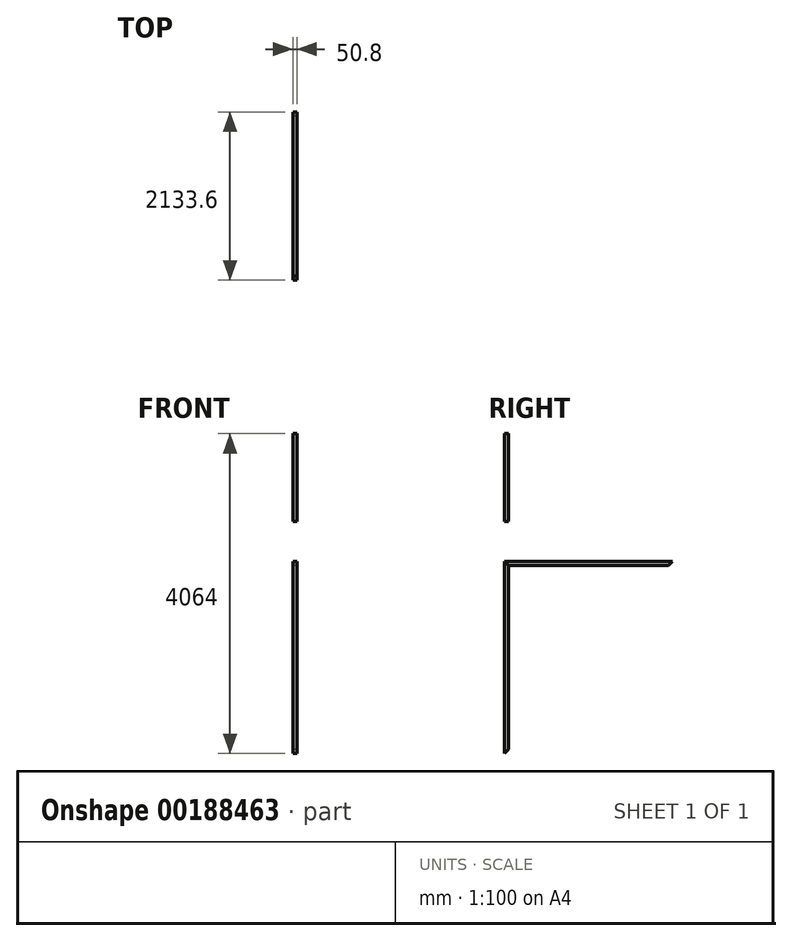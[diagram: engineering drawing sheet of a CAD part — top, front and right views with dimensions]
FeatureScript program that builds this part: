
annotation { "Feature Type Name" : "Feature", "Feature Type Description" : "" }
export const myFeature = defineFeature(function(context is Context, id is Id, definition is map)
    precondition{}
    {
        {
            var Q0;
            Q0=qCreatedBy(makeId("Right.planeOp"),FACE);
            var sketch = newSketch(context, id + "F0", { "sketchPlane" : qUnion([Q0])});
            skLineSegment(sketch, "E0.bottom", {"start": v(0, 0) * mm, "end": v(2133.6, 0) * mm});
            skLineSegment(sketch, "E0.top", {"start": v(50.8, 50.8) * mm, "end": v(2082.8, 50.8) * mm});
            skLineSegment(sketch, "E1", {"start": v(2133.6, 0) * mm, "end": v(2133.6, 2438.4) * mm});
            skLineSegment(sketch, "E2", {"start": v(2082.8, 2387.6) * mm, "end": v(2082.8, 50.8) * mm});
            skLineSegment(sketch, "E3", {"start": v(2082.8, 50.8) * mm, "end": v(2133.6, 0) * mm});
            skLineSegment(sketch, "E4", {"start": v(50.8, 50.8) * mm, "end": v(50.8, 2387.6) * mm});
            skLineSegment(sketch, "E5", {"start": v(0, 0) * mm, "end": v(50.8, 50.8) * mm});
            skLineSegment(sketch, "E6", {"start": v(0, 0) * mm, "end": v(0, 2438.4) * mm});
            skLineSegment(sketch, "E7", {"start": v(50.8, 2387.6) * mm, "end": v(2082.8, 2387.6) * mm});
            skLineSegment(sketch, "E8", {"start": v(2082.8, 2387.6) * mm, "end": v(2133.6, 2438.4) * mm});
            skLineSegment(sketch, "E9", {"start": v(50.8, 2387.6) * mm, "end": v(0, 2438.4) * mm});
            skLineSegment(sketch, "E10", {"start": v(0, 2438.4) * mm, "end": v(2133.6, 2438.4) * mm});
            skLineSegment(sketch, "E11", {"start": v(50.8, 1193.8) * mm, "end": v(2082.8, 1193.8) * mm});
            skLineSegment(sketch, "E12", {"start": v(50.8, 1244.6) * mm, "end": v(2082.8, 1244.6) * mm});
            skLineSegment(sketch, "E13", {"start": v(2590.8, 0) * mm, "end": v(2590.8, 2438.4) * mm});
            skLineSegment(sketch, "E14", {"start": v(2590.8, 2438.4) * mm, "end": v(3810, 2438.4) * mm});
            skLineSegment(sketch, "E15", {"start": v(3810, 2438.4) * mm, "end": v(3810, 0) * mm});
            skLineSegment(sketch, "E16", {"start": v(3810, 0) * mm, "end": v(2590.8, 0) * mm});
            skLineSegment(sketch, "E17.bottom", {"start": v(2641.6, 2387.6) * mm, "end": v(3759.2, 2387.6) * mm});
            skLineSegment(sketch, "E17.top", {"start": v(2641.6, 50.8) * mm, "end": v(3759.2, 50.8) * mm});
            skLineSegment(sketch, "E17.left", {"start": v(2641.6, 2438.4) * mm, "end": v(2641.6, 0) * mm});
            skLineSegment(sketch, "E17.right", {"start": v(3759.2, 2438.4) * mm, "end": v(3759.2, 0) * mm});
            skLineSegment(sketch, "E18", {"start": v(0, 2895.6) * mm, "end": v(2133.6, 2895.6) * mm});
            skLineSegment(sketch, "E19", {"start": v(0, 2895.6) * mm, "end": v(0, 4114.8) * mm});
            skLineSegment(sketch, "E20", {"start": v(0, 4114.8) * mm, "end": v(2133.6, 4114.8) * mm});
            skLineSegment(sketch, "E21", {"start": v(2133.6, 4114.8) * mm, "end": v(2133.6, 2895.6) * mm});
            skLineSegment(sketch, "E22.bottom", {"start": v(0, 4064) * mm, "end": v(2133.6, 4064) * mm});
            skLineSegment(sketch, "E22.top", {"start": v(0, 2946.4) * mm, "end": v(2133.6, 2946.4) * mm});
            skLineSegment(sketch, "E22.left", {"start": v(50.8, 4064) * mm, "end": v(50.8, 2946.4) * mm});
            skLineSegment(sketch, "E22.right", {"start": v(2082.8, 4064) * mm, "end": v(2082.8, 2946.4) * mm});
            skText(sketch, "E23", { "text": "Top", "fontName": "OpenSans-Regular.ttf"});
            skText(sketch, "E24", { "text": "Side", "fontName": "OpenSans-Regular.ttf"});
            skText(sketch, "E25", { "text": "Back", "fontName": "OpenSans-Regular.ttf"});
            skLineSegment(sketch, "E26", {"start": v(1778, 4064) * mm, "end": v(1778, 2946.4) * mm});
            skLineSegment(sketch, "E27", {"start": v(1727.2, 4064) * mm, "end": v(1727.2, 2946.4) * mm});
            skLineSegment(sketch, "E28", {"start": v(584.2, 2387.6) * mm, "end": v(584.2, 1244.6) * mm});
            skLineSegment(sketch, "E29", {"start": v(635, 2387.6) * mm, "end": v(635, 1244.6) * mm});
            skLineSegment(sketch, "E30.trimOffspring", {"start": v(635, 1193.8) * mm, "end": v(635, 50.8) * mm});
            skLineSegment(sketch, "E31.trimOffspring", {"start": v(584.2, 1193.8) * mm, "end": v(584.2, 50.8) * mm});
            skLineSegment(sketch, "E32", {"start": v(1498.6, 2387.6) * mm, "end": v(1498.6, 1244.6) * mm});
            skLineSegment(sketch, "E33", {"start": v(1549.4, 2387.6) * mm, "end": v(1549.4, 1244.6) * mm});
            skLineSegment(sketch, "E34", {"start": v(1498.6, 1193.8) * mm, "end": v(1498.6, 50.8) * mm});
            skLineSegment(sketch, "E35", {"start": v(1549.4, 1193.8) * mm, "end": v(1549.4, 50.8) * mm});
            skLineSegment(sketch, "E36", {"start": v(666.83, 1193.8) * mm, "end": v(1498.6, 92.93) * mm});
            skLineSegment(sketch, "E37", {"start": v(635, 1151.67) * mm, "end": v(1466.77, 50.8) * mm});
            skLineSegment(sketch, "E38", {"start": v(635, 1286.73) * mm, "end": v(1466.77, 2387.6) * mm});
            skLineSegment(sketch, "E39", {"start": v(666.83, 1244.6) * mm, "end": v(1498.6, 2345.47) * mm});
            skLineSegment(sketch, "E40", {"start": v(2641.6, 1549.4) * mm, "end": v(3759.2, 1549.4) * mm});
            skLineSegment(sketch, "E41", {"start": v(2641.6, 889) * mm, "end": v(3759.2, 889) * mm});
            skLineSegment(sketch, "E42", {"start": v(2641.6, 1498.6) * mm, "end": v(3759.2, 1498.6) * mm});
            skLineSegment(sketch, "E43", {"start": v(2641.6, 939.8) * mm, "end": v(3759.2, 939.8) * mm});
            skLineSegment(sketch, "E44", {"start": v(2641.6, 1581.15) * mm, "end": v(3716.87, 2387.6) * mm});
            skLineSegment(sketch, "E45", {"start": v(3759.2, 2355.85) * mm, "end": v(2683.93, 1549.4) * mm});
            skLineSegment(sketch, "E46", {"start": v(889, 4064) * mm, "end": v(889, 2946.4) * mm});
            skLineSegment(sketch, "E47", {"start": v(939.8, 4064) * mm, "end": v(939.8, 2946.4) * mm});
            skLineSegment(sketch, "E48", {"start": v(2082.8, 711.2) * mm, "end": v(1549.4, 711.2) * mm});
            skLineSegment(sketch, "E49", {"start": v(1549.4, 660.4) * mm, "end": v(2082.8, 660.4) * mm});
            skLineSegment(sketch, "E50.trimOffspring", {"start": v(2641.6, 660.4) * mm, "end": v(3759.2, 660.4) * mm});
            skLineSegment(sketch, "E51", {"start": v(2641.6, 711.2) * mm, "end": v(3759.2, 711.2) * mm});
            skLineSegment(sketch, "E52", {"start": v(2641.6, 631.47) * mm, "end": v(3706.16, 50.8) * mm});
            skLineSegment(sketch, "E53", {"start": v(2694.64, 660.4) * mm, "end": v(3759.2, 79.73) * mm});
            skLineSegment(sketch, "E54", {"start": v(2698.4, 1498.6) * mm, "end": v(3759.2, 968.2) * mm});
            skLineSegment(sketch, "E55", {"start": v(2641.6, 1470.2) * mm, "end": v(3702.4, 939.8) * mm});
            const initialGuessF0  = {"E23": [0.8897, 4.24616, 1, 0, 0.17145], "E24": [0.77467, -0.30196, 1, 0, 0.17145], "E25": [3.0356, -0.28653, 1, 0, 0.17145]};
            skSetInitialGuess(sketch, initialGuessF0);
            skSolve(sketch);
        }
        {
            var Q0;
            Q0=qCreatedBy(makeId("Right.planeOp"),FACE);
            var sketch = newSketch(context, id + "F1", { "sketchPlane" : qUnion([Q0])});
            skLineSegment(sketch, "E56", {"start": v(0, 2438.4) * mm, "end": v(0, 0) * mm});
            skLineSegment(sketch, "E57", {"start": v(0, 0) * mm, "end": v(50.8, 50.8) * mm});
            skLineSegment(sketch, "E58", {"start": v(50.8, 50.8) * mm, "end": v(50.8, 2387.6) * mm});
            skLineSegment(sketch, "E59", {"start": v(50.8, 2387.6) * mm, "end": v(0, 2438.4) * mm});
            skSolve(sketch);
        }
        {
            var Q0;
            Q0 = qSketchRegion(id + "F1", true);
            extrude(context, id + "F2", {"entities" : qUnion([Q0]), "depth" : 50.8 * mm});
        }
        {
            var Q0;
            Q0=qCreatedBy(makeId("Right.planeOp"),FACE);
            var sketch = newSketch(context, id + "F3", { "sketchPlane" : qUnion([Q0])});
            skLineSegment(sketch, "E60", {"start": v(0, 2438.4) * mm, "end": v(2133.6, 2438.4) * mm});
            skLineSegment(sketch, "E61", {"start": v(2133.6, 2438.4) * mm, "end": v(2082.8, 2387.6) * mm});
            skLineSegment(sketch, "E62", {"start": v(2082.8, 2387.6) * mm, "end": v(50.8, 2387.6) * mm});
            skLineSegment(sketch, "E63", {"start": v(50.8, 2387.6) * mm, "end": v(0, 2438.4) * mm});
            skSolve(sketch);
        }
        {
            var Q0;
            Q0 = qSketchRegion(id + "F3", true);
            extrude(context, id + "F4", {"entities" : qUnion([Q0]), "depth" : 50.8 * mm});
        }
        {
            var Q0;
            Q0=qCreatedBy(makeId("Right.planeOp"),FACE);
            var sketch = newSketch(context, id + "F5", { "sketchPlane" : qUnion([Q0])});
            skLineSegment(sketch, "E64", {"start": v(0, 4064) * mm, "end": v(50.8, 4064) * mm});
            skLineSegment(sketch, "E65", {"start": v(50.8, 4064) * mm, "end": v(50.8, 2946.4) * mm});
            skLineSegment(sketch, "E66", {"start": v(50.8, 2946.4) * mm, "end": v(0, 2946.4) * mm});
            skLineSegment(sketch, "E67", {"start": v(0, 2946.4) * mm, "end": v(0, 4064) * mm});
            skSolve(sketch);
        }
        {
            var Q0;
            Q0 = qSketchRegion(id + "F5", true);
            extrude(context, id + "F6", {"entities" : qUnion([Q0]), "depth" : 50.8 * mm});
        }
    });
